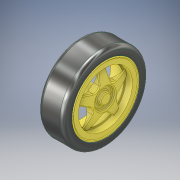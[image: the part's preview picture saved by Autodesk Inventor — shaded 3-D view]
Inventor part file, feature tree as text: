
AUTODESK INVENTOR PART (.ipt)
format: ipt  version: 2017 (Build 210142000, 142)  size: 552,960 bytes
history: mixed  units: in
note: dims shown in document units (in); Inventor stores cm internally (conversion verified against a paired STEP export)
features: revolve x2, other x1, imported_body x1
ambient origin geometry x8: Origin, YZ Plane, XZ Plane, XY Plane, X Axis, Y Axis, Z Axis, Center Point
bodies: Solid1 (imported_parasolid), Solid2 (imported_parasolid), Solid3 (imported_parasolid)
feature tree (4):
  revolve  "Revolución3"  [1 undecoded]
  revolve  "Revolución4"  [1 undecoded]
  other  "Cortar-Extruir2"
  imported_body  NMx_Import_Brep_tag  [imported B-rep: ~15 faces, bbox_mm=None]
note: 2 required parameter values undecoded (feature->parameter linkage not recoverable at this tier; creation-order binding heuristic only, values carry confidence <= 0.55)
